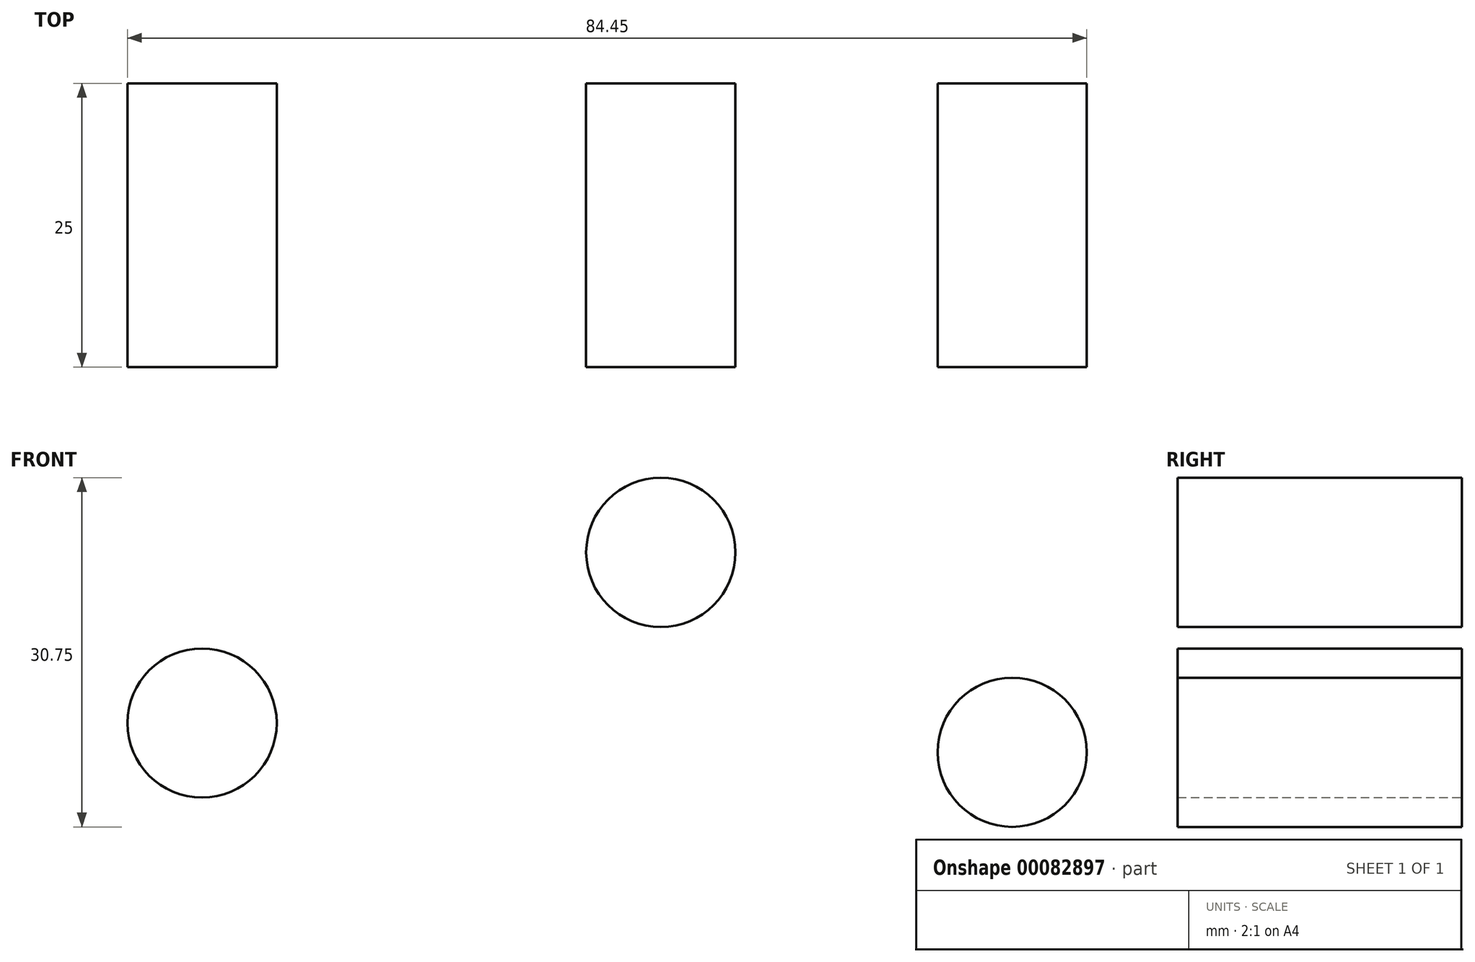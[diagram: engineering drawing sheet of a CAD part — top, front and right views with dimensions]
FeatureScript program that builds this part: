
annotation { "Feature Type Name" : "Feature", "Feature Type Description" : "" }
export const myFeature = defineFeature(function(context is Context, id is Id, definition is map)
    precondition{}
    {
        {
            var Q0;
            Q0=qCreatedBy(makeId("Front.planeOp"),FACE);
            var sketch = newSketch(context, id + "F0", { "sketchPlane" : qUnion([Q0])});
            skCircle(sketch, "E0", {"center": v(-27.28, 19.76) * mm, "radius": 6.57 * mm});
            skCircle(sketch, "E1", {"center": v(13.1, 34.8) * mm, "radius": 6.57 * mm});
            skCircle(sketch, "E2", {"center": v(44.03, 17.18) * mm, "radius": 6.57 * mm});
            skSolve(sketch);
        }
        {
            var Q0;
            Q0 = qSketchRegion(id + "F0", true);
            extrude(context, id + "F1", {"entities" : qUnion([Q0]), "depth" : 25 * mm});
        }
    });
